# Revit family: Washroom-Accessories_Baby-Changer_Rubbermaid
name_source: partatom
category: Generic Models
units: mm (PartAtom-declared; Revit-internal decimal feet)

## family parameters
Can host rebar = No
Cut with Voids When Loaded = No
Host = Face
Maintain Annotation Orientation = No
Part Type = Normal
Room Calculation Point = No
Round Connector Dimension = Use Diameter
Shared = No

## types (2) — shared parameters
CAD Details = https://www.arcat.com
Default Elevation = 48 "
Height = 4 "
Keynote = 10 28 13
Material = Rubbermaid_Plastic-Light Platinum
Product Page URL = https://www.arcat.com
Specification = https://www.arcat.com
URL = https://www.rubbermaidcommercial.com

## per-type parameters (varying)
| type | Angel | Close | Length | Open | Width |
| Baby Changing Station_Vertical | 0.00° | No | 23 " | Yes | 34.1 " |
| Baby Changing Station_Horizontal | 90.00° | Yes | 34.25 " | No | 21.5 " |

type visibility flags: 2 boolean params named "<type name>" — each type sets only its own to Yes (folded from table)

## geometry (parser evidence)
native form markers: Sweep x8
no freeform markers — native parametric forms only
